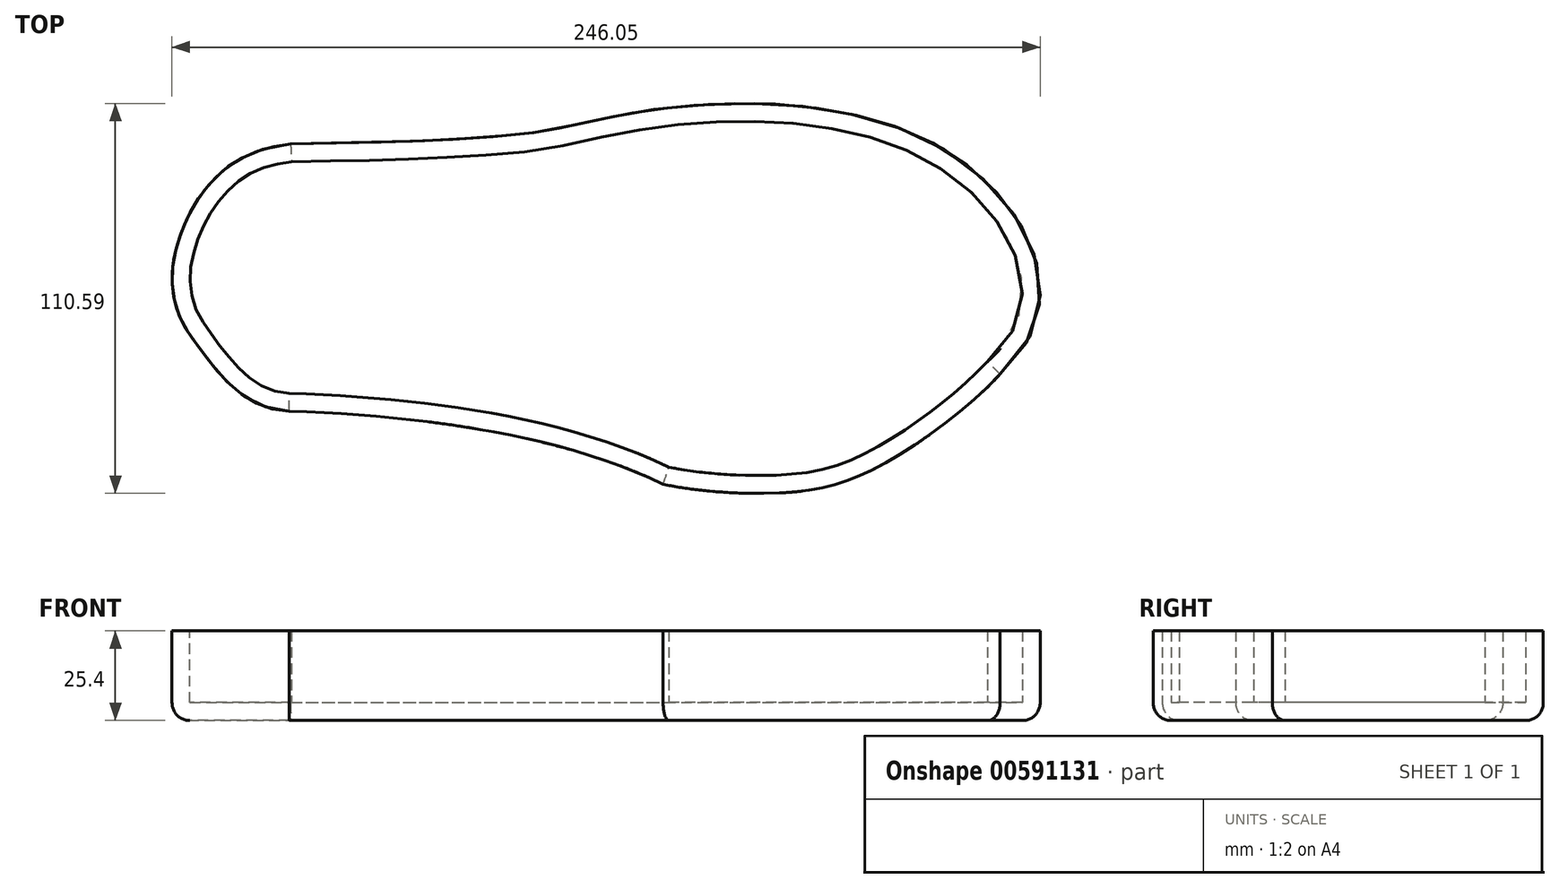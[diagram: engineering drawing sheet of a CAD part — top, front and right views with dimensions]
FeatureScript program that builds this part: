
annotation { "Feature Type Name" : "Feature", "Feature Type Description" : "" }
export const myFeature = defineFeature(function(context is Context, id is Id, definition is map)
    precondition{}
    {
        {
            var Q0;
            Q0=qCreatedBy(makeId("Top.planeOp"),FACE);
            var sketch = newSketch(context, id + "F0", { "sketchPlane" : qUnion([Q0])});
            skFitSpline(sketch, "E0", {"points": [v(-110.01, 75.8) * mm, v(-136.92, 59.03) * mm, v(-142.1, 47.15) * mm, v(-143.62, 37.1) * mm, v(-141.49, 26.76) * mm, v(-136.32, 18.54) * mm, v(-110.45, 0) * mm], "startDerivative": vector(-198.97, -19.9) * mm, "endDerivative": vector(165.81, 0) * mm});
            skFitSpline(sketch, "E1", {"points": [v(-110.45, 0) * mm, v(-52.91, -5.8) * mm, v(-4.46, -20.75) * mm], "startDerivative": vector(114.33, -4.18) * mm, "endDerivative": vector(89.85, -43.95) * mm});
            skFitSpline(sketch, "E2", {"points": [v(-110.01, 75.8) * mm, v(-39.78, 79.17) * mm, v(-12.33, 84.7) * mm, v(75.5, 73.97) * mm, v(91.05, 10.43) * mm], "startDerivative": vector(296.77, 4.3) * mm, "endDerivative": vector(-263.21, -233.32) * mm});
            skFitSpline(sketch, "E3", {"points": [v(91.05, 10.43) * mm, v(56.27, -15.9) * mm, v(32.66, -22.93) * mm, v(-4.46, -20.75) * mm], "startDerivative": vector(-78.19, -83.71) * mm, "endDerivative": vector(-102, 21.09) * mm});
            skSolve(sketch);
        }
        {
            var Q0;
            Q0 = qSketchRegion(id + "F0", true);
            extrude(context, id + "F1", {"entities" : qUnion([Q0]), "depth" : 25.4 * mm, "offsetDistance" : 25.4 * mm, "symmetric" : true});
        }
        {
            var Q0;
            Q0=makeQuery(id+"F1.opExtrude","CAP_FACE",FACE,{"disambiguationData":[OSD([sQuery(id+"F0.wireOp",EDGE,"E0"),sQuery(id+"F0.wireOp",EDGE,"E1"),sQuery(id+"F0.wireOp",EDGE,"E2"),sQuery(id+"F0.wireOp",EDGE,"E3")])],"isStart":false});
            shell(context, id + "F2", {"entities" : qUnion([Q0]), "thickness" : 5.08 * mm});
        }
        {
            var Q0;
            Q0=makeQuery(id+"F1.opExtrude","CAP_EDGE",EDGE,{"disambiguationData":[OSD([sQuery(id+"F0.wireOp",EDGE,"E1")])],"isStart":true});
            var Q1;
            Q1=makeQuery(id+"F1.opExtrude","CAP_EDGE",EDGE,{"disambiguationData":[OSD([sQuery(id+"F0.wireOp",EDGE,"E3")])],"isStart":true});
            var Q2;
            Q2=makeQuery(id+"F1.opExtrude","CAP_EDGE",EDGE,{"disambiguationData":[OSD([sQuery(id+"F0.wireOp",EDGE,"E2")])],"isStart":true});
            var Q3;
            Q3=makeQuery(id+"F1.opExtrude","CAP_EDGE",EDGE,{"disambiguationData":[OSD([sQuery(id+"F0.wireOp",EDGE,"E0")])],"isStart":true});
            fillet(context, id + "F3", {"entities" : qUnion([Q0, Q1, Q2, Q3]), "radius" : 5.08 * mm, "tangentPropagation" : true, "allowEdgeOverflow" : false});
        }
    });
